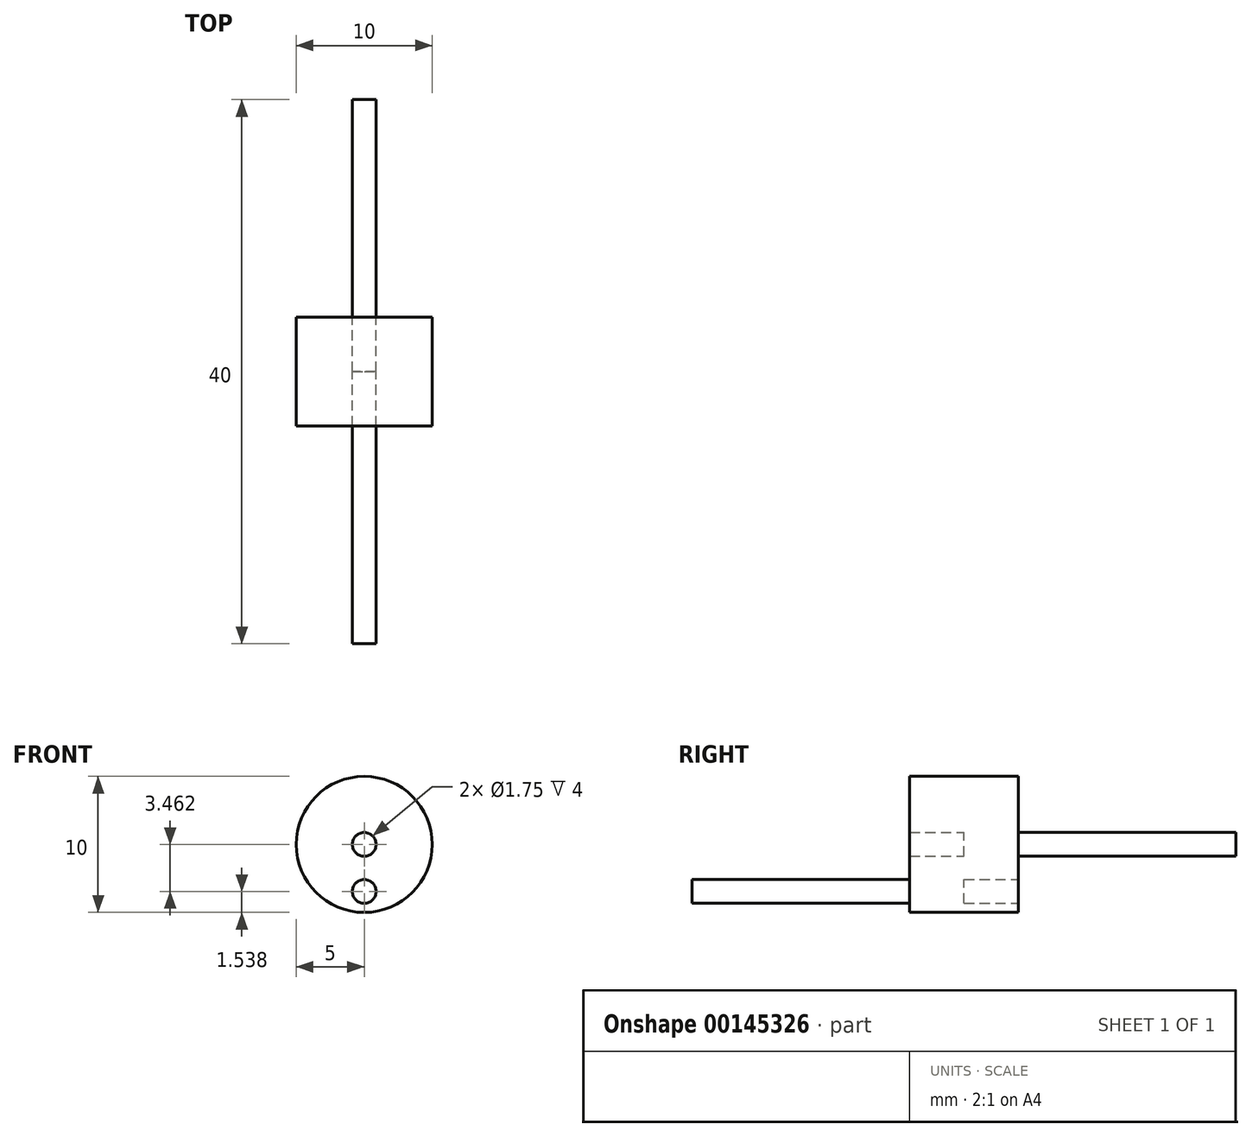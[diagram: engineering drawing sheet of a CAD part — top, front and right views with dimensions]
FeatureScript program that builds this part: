
annotation { "Feature Type Name" : "Feature", "Feature Type Description" : "" }
export const myFeature = defineFeature(function(context is Context, id is Id, definition is map)
    precondition{}
    {
        {
            var Q0;
            Q0=qCreatedBy(makeId("Front.planeOp"),FACE);
            var sketch = newSketch(context, id + "F0", { "sketchPlane" : qUnion([Q0])});
            skCircle(sketch, "E0", {"center": v(0, 0) * mm, "radius": 5 * mm});
            skCircle(sketch, "E1", {"center": v(0, 0) * mm, "radius": 0.87 * mm});
            skCircle(sketch, "E2", {"center": v(0, -3.46) * mm, "radius": 0.88 * mm});
            skSolve(sketch);
        }
        {
            var Q0;
            Q0=makeQuery(id+"F0.imprint","IMPRINT",FACE,{"disambiguationData":[TD([[makeQuery(id+"F0.imprint","IMPRINT",EDGE,{"derivedFrom":sQuery(id+"F0.wireOp",EDGE,"E0")}),1.0]])]});
            extrude(context, id + "F1", {"entities" : qUnion([Q0]), "endBound" : BoundingType.SYMMETRIC, "depth" : 8 * mm});
        }
        {
            var Q0;
            Q0=makeQuery(id+"F0.imprint","IMPRINT",FACE,{"disambiguationData":[TD([[makeQuery(id+"F0.imprint","IMPRINT",EDGE,{"derivedFrom":sQuery(id+"F0.wireOp",EDGE,"E1")}),1.0]])]});
            extrude(context, id + "F2", {"entities" : qUnion([Q0]), "operationType" : NewBodyOperationType.ADD, "oppositeDirection" : true, "depth" : 20 * mm});
        }
        {
            var Q0;
            Q0=makeQuery(id+"F0.imprint","IMPRINT",FACE,{"disambiguationData":[TD([[makeQuery(id+"F0.imprint","IMPRINT",EDGE,{"derivedFrom":sQuery(id+"F0.wireOp",EDGE,"E2")}),1.0]])]});
            extrude(context, id + "F3", {"entities" : qUnion([Q0]), "operationType" : NewBodyOperationType.ADD, "depth" : 20 * mm});
        }
    });
